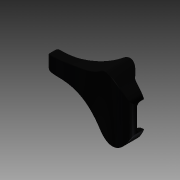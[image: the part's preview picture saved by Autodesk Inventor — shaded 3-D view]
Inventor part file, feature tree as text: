
AUTODESK INVENTOR PART (.ipt)
format: ipt  version: 2013 (Build 170138000, 138)  size: 1,144,832 bytes
history: native  units: mm
features: extrude x9, fillet x8, sketch x6, other x3, plane x3, chamfer x2, hole x1, mirror x1
ambient origin geometry x8: Origin, YZ Plane, XZ Plane, XY Plane, X Axis, Y Axis, Z Axis, Center Point
feature tree (33):
  other  "Sólido1"
  sketch  "Boceto1"  dims[d0=1.0mm d3=26.0mm]
  extrude  "Extrusión1"  Depth=26.0mm
  sketch  "Boceto3"  dims[d16=8.0mm d17=0.0mm d20=3.5mm]
  extrude  "Extrusión2"  Depth=8.0mm
  other  "Suprimir cara1"
  other  "Suprimir cara2"
  extrude  "Extrusión3"  Depth=3.5mm
  extrude  "Extrusión4"  Depth=1.0mm
  fillet  "Empalme1"  Radius=1.0mm
  fillet  "Empalme2"  Radius=1.5mm
  fillet  "Empalme3"  Radius=20.0mm
  plane  "Plano de trabajo1"
  fillet  "Empalme4"  Radius=2.0mm
  fillet  "Empalme5"  Radius=20.0mm
  fillet  "Empalme6"  Radius=1.0mm
  fillet  "Empalme7"  Radius=0.45mm
  fillet  "Empalme8"  Radius=1.0mm
  plane  "Plano de trabajo2"
  sketch  "Boceto5"  dims[d29=1.0mm d30=1.0mm d37=1.0mm d38=1.5mm]
  extrude  "Extrusión5"  Depth=2.0mm
  extrude  "Extrusión6"  Depth=0.15mm
  plane  "Plano de trabajo3"
  extrude  "Extrusión7"  Depth=15.0mm
  extrude  "Extrusión8"  Depth=0.1mm
  extrude  "Extrusión9"  [1 undecoded]
  hole  "Hole2"  [1 undecoded]
  mirror  "Simetría1"
  chamfer  "Chaflán2"  Distance=22.0mm
  chamfer  "Chaflán3"  Distance=0.5mm
  sketch  "Boceto2"  dims[d9=4.0mm d10=8.0mm]
  sketch  "Boceto8"  dims[d40=3.0mm d41=6.0mm d42=0.0mm d43=0.0mm d44=20.0mm d45=0.0mm d46=2.0mm d47=20.0mm d48=0.0mm d49=1.0mm d50=0.45mm d51=1.0mm]
  sketch  "Boceto9"  dims[d52=-8.0mm d53=20.0mm d54=2.0mm d55=0.15mm d56=15.0mm d57=0.1mm d58=-3.0mm d59=8.0mm d60=22.0mm d61=0.5mm d62=1.0mm d63=2.5mm d64=0.5mm d65=1.0mm d66=1.5mm d67=2.0mm d68=1.0mm d69=0.0mm d70=0.0mm d71=0.5mm d72=1.0mm d73=0.0mm d74=0.0mm d75=1.0mm d76=8.0mm d77=3.0mm d78=1.0mm d79=1.5mm d80=1.2mm d81=0.0mm d93=1.5mm d94=0.0mm d95=0.5mm d96=2.0mm d97=1.0mm d98=0.0mm d99=0.0mm d100=0.6mm d101=0.6mm d102=6.0mm d103=4.0mm d104=2.0mm d105=90.0deg d106=1.5mm d107=0.0mm d108=0.5mm d121=0.05mm d122=0.05mm d123=2.0mm d124=45.0deg d125=0.1mm d126=2.0mm d127=45.0deg]
note: 2 required parameter values undecoded (feature->parameter linkage not recoverable at this tier; creation-order binding heuristic only, values carry confidence <= 0.55)
